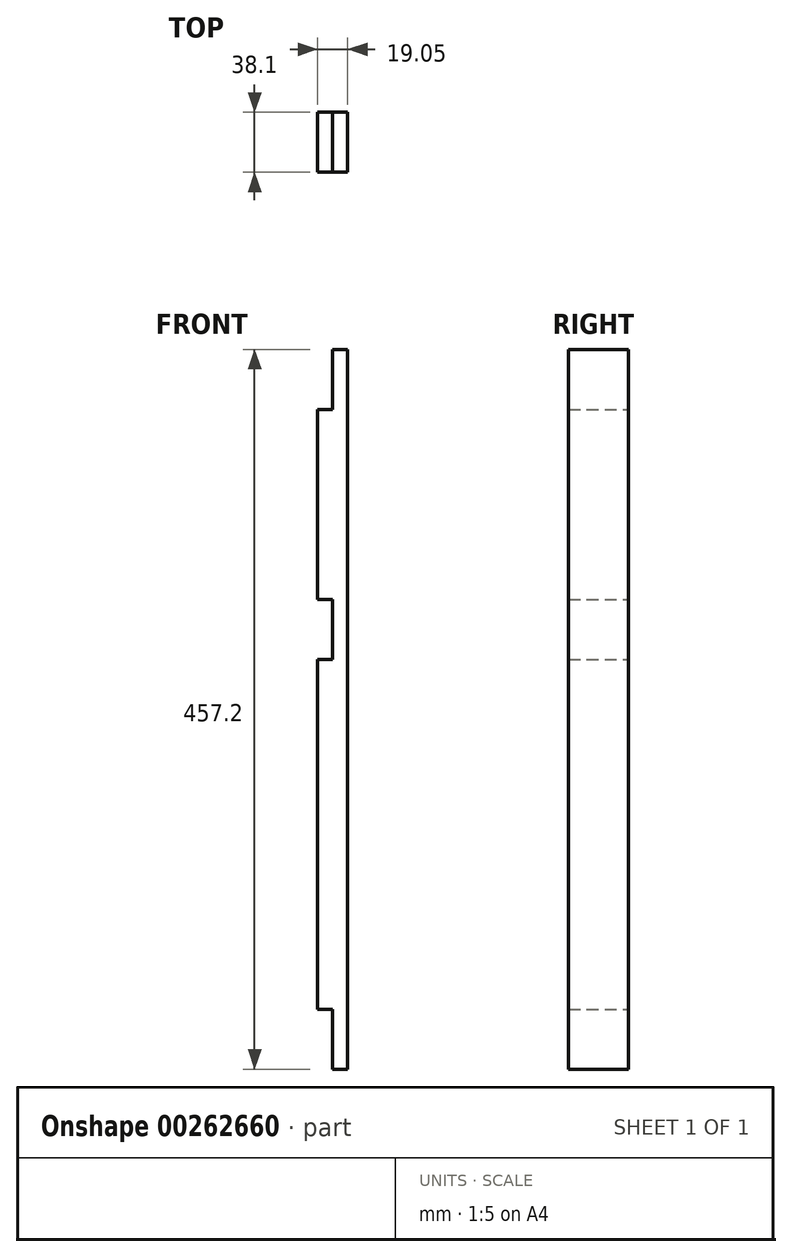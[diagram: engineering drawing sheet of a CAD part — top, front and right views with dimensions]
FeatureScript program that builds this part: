
annotation { "Feature Type Name" : "Feature", "Feature Type Description" : "" }
export const myFeature = defineFeature(function(context is Context, id is Id, definition is map)
    precondition{}
    {
        {
            var Q0;
            Q0=qCreatedBy(makeId("Front.planeOp"),FACE);
            var sketch = newSketch(context, id + "F0", { "sketchPlane" : qUnion([Q0])});
            skLineSegment(sketch, "E0", {"start": v(0, 0) * mm, "end": v(0, -457.2) * mm});
            skLineSegment(sketch, "E1", {"start": v(0, 0) * mm, "end": v(-9.52, 0) * mm});
            skLineSegment(sketch, "E2", {"start": v(-9.52, 0) * mm, "end": v(-9.52, -38.1) * mm});
            skLineSegment(sketch, "E3", {"start": v(-9.52, -38.1) * mm, "end": v(-19.05, -38.1) * mm});
            skLineSegment(sketch, "E4", {"start": v(-19.05, -38.1) * mm, "end": v(-19.05, -158.72) * mm});
            skLineSegment(sketch, "E5", {"start": v(-19.05, -158.72) * mm, "end": v(-9.52, -158.72) * mm});
            skLineSegment(sketch, "E6", {"start": v(-9.52, -158.72) * mm, "end": v(-9.52, -196.82) * mm});
            skLineSegment(sketch, "E7", {"start": v(-9.52, -196.82) * mm, "end": v(-19.05, -196.82) * mm});
            skLineSegment(sketch, "E8", {"start": v(-19.05, -196.82) * mm, "end": v(-19.05, -419.1) * mm});
            skLineSegment(sketch, "E9", {"start": v(-19.05, -419.1) * mm, "end": v(-9.52, -419.1) * mm});
            skLineSegment(sketch, "E10", {"start": v(-9.52, -419.1) * mm, "end": v(-9.52, -457.2) * mm});
            skLineSegment(sketch, "E11", {"start": v(-9.52, -457.2) * mm, "end": v(0, -457.2) * mm});
            skSolve(sketch);
        }
        {
            var Q0;
            Q0=makeQuery(id+"F0.imprint","IMPRINT",FACE,{"disambiguationData":[TD([[makeQuery(id+"F0.imprint","IMPRINT",EDGE,{"derivedFrom":sQuery(id+"F0.wireOp",EDGE,"E0")}),-1.0]])]});
            extrude(context, id + "F1", {"entities" : qUnion([Q0]), "depth" : 38.1 * mm});
        }
    });
